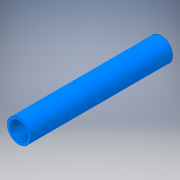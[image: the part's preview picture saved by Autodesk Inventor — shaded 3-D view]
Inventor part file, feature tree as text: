
AUTODESK INVENTOR PART (.ipt)
format: ipt  version: 2018 (Build 220112000, 112)  size: 109,056 bytes
history: native  units: in
note: dims shown in document units (in); Inventor stores cm internally (conversion verified against a paired STEP export)
features: extrude x1, sketch x1
ambient origin geometry x8: Origin, YZ Plane, XZ Plane, XY Plane, X Axis, Y Axis, Z Axis, Center Point
bodies: Solid1 (feature_tree)
feature tree (2):
  extrude  "Extrusion1"  Depth=8.0in
  sketch  "Sketch1"  dims[d0=1.315in d1=1.0in d2=8.0in d3=0.0in]
